# Revit family: Lighting-Pendant-Cooper-Ametrix-Asyx-2-SP-DP-LED
name_source: partatom
category: Lighting Fixtures
revit_build: Autodesk Revit 2014 (Build: 20130308_1515(x64)
units: mm (PartAtom-declared; Revit-internal decimal feet)

## types (1)
- Lighting-Pendant-Cooper-Ametrix-Asyx-2-SP-DP-LED
    120 Volt = Yes
    24 inch Pendant Stem = No
    30 inch Pendant Stem = No
    36 inch Pendant Stem = Yes
    48 inch Pendant Stem = No
    Apparent Load = 0 VA
    Assembly Code = D5020200
    Color Filter = 16777215
    Connector Description = Power In
    Default Elevation = 0' - 0"
    Description = Asymmetric LED Direct & Indirect
    Dimming Lamp Color Temperature Shift = <None>
    Dual Pendant = Yes
    Finish = Finish - Cooper Industries - White
    Fins Array = 16
    Fins Width = 1' - 0 15/16"
    Fixture Width = 1' - 2 1/8"
    Frequency = 50 Hz
    Housing Depth = 0' - 2 1/2"
    Housing Height = 1' - 0 3/4"
    Housing Width = 1' - 2 3/16"
    Lamp = LED
    Load Classification = Lighting
    Manufacturer = Cooper Lighting
    Model = SP & DP
    Mounting = Pendant
    Mounting Plate = 0' - 8"
    Number of LightBARs = 3
    Offset = 2' - 11"
    Pendant Length = 3' - 0"
    Photometric Web File = ASYX-S-L-F-X-X-L27-1-STD-UNV.ies
    Power (Wattage) = 70 W
    Power Factor = 0.9
    Tilt Angle = 90.00°
    Type Comments = Single & Dual Pendant
    URL = www.eaton.com/lighting
    Voltage = 120 V

## geometry (parser evidence)
native form markers: Blend x2, Sweep x7
no freeform markers — native parametric forms only
